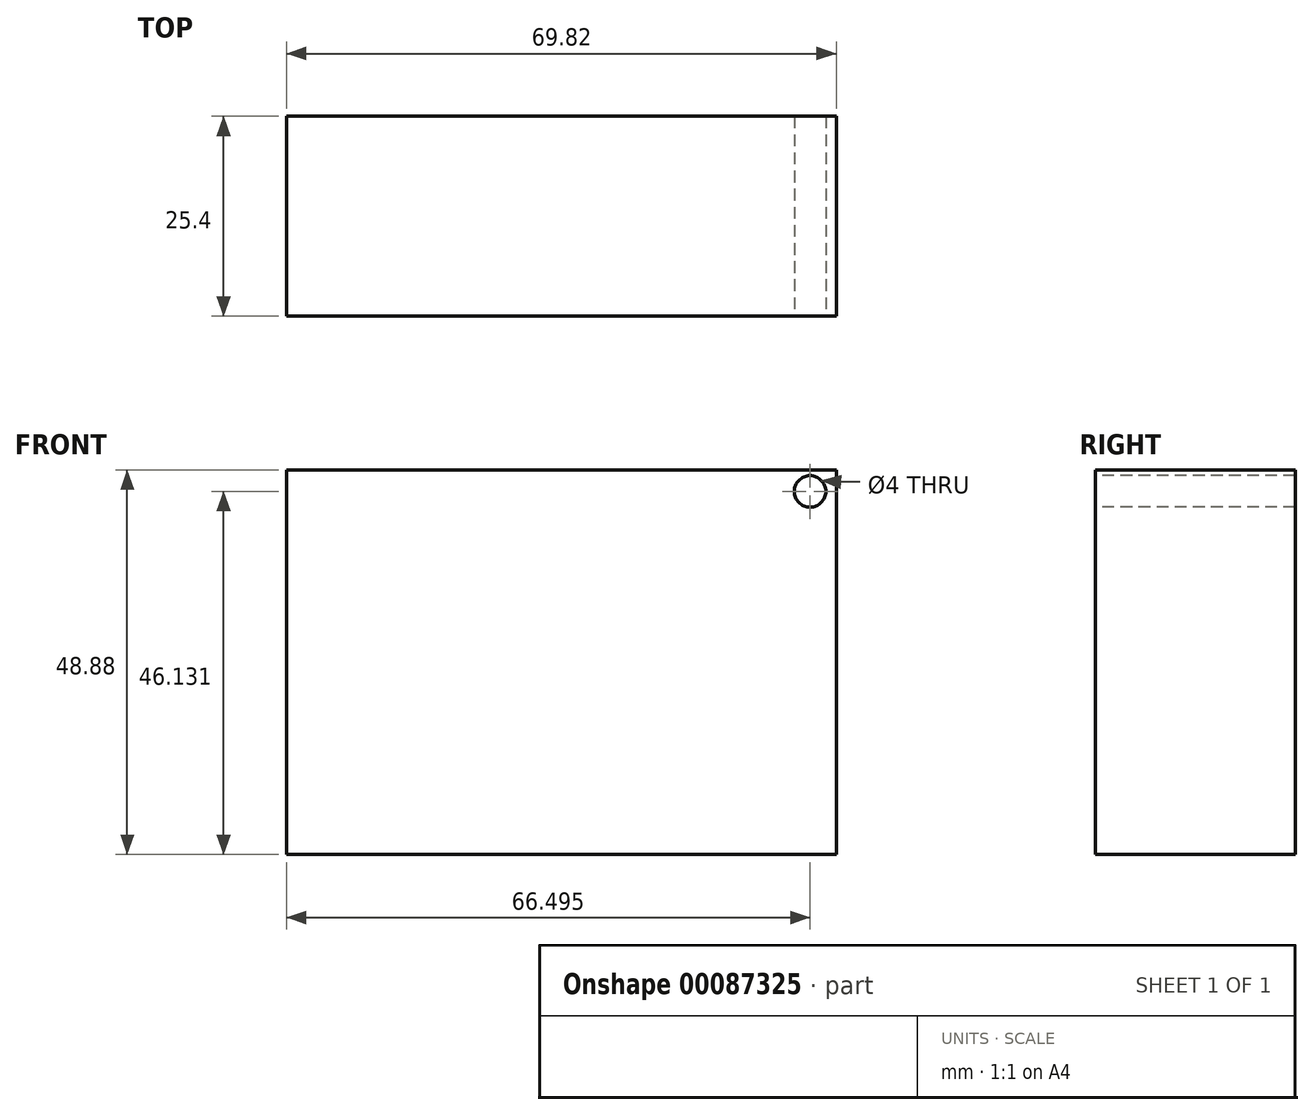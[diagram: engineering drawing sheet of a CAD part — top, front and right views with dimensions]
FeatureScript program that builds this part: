
annotation { "Feature Type Name" : "Feature", "Feature Type Description" : "" }
export const myFeature = defineFeature(function(context is Context, id is Id, definition is map)
    precondition{}
    {
        {
            var Q0;
            Q0=qCreatedBy(makeId("Front.planeOp"),FACE);
            var sketch = newSketch(context, id + "F0", { "sketchPlane" : qUnion([Q0])});
            skLineSegment(sketch, "E0.bottom", {"start": v(30.96, 38.03) * mm, "end": v(-38.86, 38.03) * mm});
            skLineSegment(sketch, "E0.top", {"start": v(30.96, -10.85) * mm, "end": v(-38.86, -10.85) * mm});
            skLineSegment(sketch, "E0.left", {"start": v(30.96, 38.03) * mm, "end": v(30.96, -10.85) * mm});
            skLineSegment(sketch, "E0.right", {"start": v(-38.86, 38.03) * mm, "end": v(-38.86, -10.85) * mm});
            skSolve(sketch);
        }
        {
            var Q0;
            Q0=makeQuery(id+"F0.imprint","IMPRINT",FACE,{"disambiguationData":[TD([[makeQuery(id+"F0.imprint","IMPRINT",EDGE,{"derivedFrom":sQuery(id+"F0.wireOp",EDGE,"E0.bottom")}),1.0]])]});
            extrude(context, id + "F3", {"entities" : qUnion([Q0]), "depth" : 25.4 * mm});
        }
        {
            var Q0;
            Q0=makeQuery(id+"F3.opExtrude","CAP_FACE",FACE,{"disambiguationData":[OSD([sQuery(id+"F0.wireOp",EDGE,"E0.bottom"),sQuery(id+"F0.wireOp",EDGE,"E0.top"),sQuery(id+"F0.wireOp",EDGE,"E0.left"),sQuery(id+"F0.wireOp",EDGE,"E0.right")])],"isStart":false});
            var sketch = newSketch(context, id + "F1", { "sketchPlane" : qUnion([Q0])});
            skSolve(sketch);
        }
        {
            var Q0;
            Q0=makeQuery(id+"F1.imprint","IMPRINT",FACE,{"disambiguationData":[TD([[makeQuery(id+"F1.imprint","IMPRINT",EDGE,{"derivedFrom":makeQuery(id+"F3.opExtrude","CAP_EDGE",EDGE,{"disambiguationData":[OSD([sQuery(id+"F0.wireOp",EDGE,"E0.bottom")])],"isStart":false})}),1.0]])]});
            var sketch = newSketch(context, id + "F2", { "sketchPlane" : qUnion([Q0])});
            skCircle(sketch, "E1", {"center": v(27.63, 35.28) * mm, "radius": 2.18 * mm});
            skSolve(sketch);
        }
        {
            var Q0;
            Q0=sQuery(id+"F2.wireOp",VERTEX,"E1.center");
            var Q1;
            Q1=makeQuery(id+"F3.opExtrude","SWEPT_BODY",BODY,{"disambiguationData":[OSD([sQuery(id+"F0.wireOp",EDGE,"E0.bottom"),sQuery(id+"F0.wireOp",EDGE,"E0.top"),sQuery(id+"F0.wireOp",EDGE,"E0.left"),sQuery(id+"F0.wireOp",EDGE,"E0.right")])]});
            hole(context, id + "F4", {"style" : HoleStyle.SIMPLE, "endStyle" : HoleEndStyle.THROUGH, "holeDiameter" : 4 * mm, "locations" : qUnion([Q0]), "scope" : qUnion([Q1]), "isTappedThrough" : true});
        }
    });
